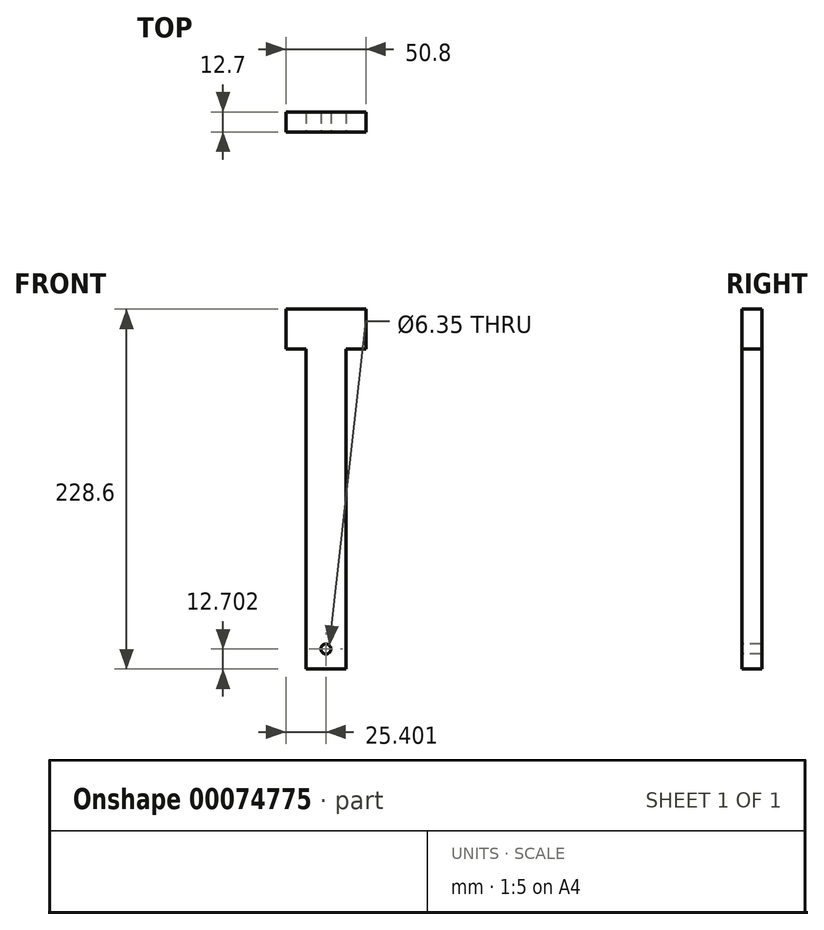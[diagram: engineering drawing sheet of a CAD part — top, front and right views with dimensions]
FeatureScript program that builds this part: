
annotation { "Feature Type Name" : "Feature", "Feature Type Description" : "" }
export const myFeature = defineFeature(function(context is Context, id is Id, definition is map)
    precondition{}
    {
        {
            var Q0;
            Q0=qCreatedBy(makeId("Front.planeOp"),FACE);
            var sketch = newSketch(context, id + "F0", { "sketchPlane" : qUnion([Q0])});
            skLineSegment(sketch, "E0", {"start": v(-30.38, -174.97) * mm, "end": v(-4.98, -174.97) * mm});
            skLineSegment(sketch, "E1", {"start": v(-4.98, -174.97) * mm, "end": v(-4.98, 28.23) * mm});
            skLineSegment(sketch, "E2", {"start": v(-4.98, 28.23) * mm, "end": v(7.72, 28.23) * mm});
            skLineSegment(sketch, "E3", {"start": v(7.72, 28.23) * mm, "end": v(7.72, 53.63) * mm});
            skLineSegment(sketch, "E4", {"start": v(7.72, 53.63) * mm, "end": v(-43.08, 53.63) * mm});
            skLineSegment(sketch, "E5", {"start": v(-43.08, 53.63) * mm, "end": v(-43.08, 28.23) * mm});
            skLineSegment(sketch, "E6", {"start": v(-43.08, 28.23) * mm, "end": v(-30.38, 28.23) * mm});
            skLineSegment(sketch, "E7", {"start": v(-30.38, 28.23) * mm, "end": v(-30.38, -174.97) * mm});
            skSolve(sketch);
        }
        {
            var Q0;
            Q0=makeQuery(id+"F0.imprint","IMPRINT",FACE,{"disambiguationData":[TD([[makeQuery(id+"F0.imprint","IMPRINT",EDGE,{"derivedFrom":sQuery(id+"F0.wireOp",EDGE,"E0")}),1.0]])]});
            extrude(context, id + "F1", {"entities" : qUnion([Q0]), "oppositeDirection" : true, "depth" : 12.7 * mm});
        }
        {
            var Q0;
            Q0=makeQuery(id+"F1.opExtrude","CAP_FACE",FACE,{"disambiguationData":[OSD([sQuery(id+"F0.wireOp",EDGE,"E0"),sQuery(id+"F0.wireOp",EDGE,"E1"),sQuery(id+"F0.wireOp",EDGE,"E2"),sQuery(id+"F0.wireOp",EDGE,"E3"),sQuery(id+"F0.wireOp",EDGE,"E4"),sQuery(id+"F0.wireOp",EDGE,"E5"),sQuery(id+"F0.wireOp",EDGE,"E6"),sQuery(id+"F0.wireOp",EDGE,"E7")])],"isStart":true});
            var sketch = newSketch(context, id + "F2", { "sketchPlane" : qUnion([Q0])});
            skPoint(sketch, "E8", {"position": v(-17.68, -162.27) * mm});
            skPoint(sketch, "E8.positionSnap0", {"position": v(-17.68, -174.97) * mm});
            skSolve(sketch);
        }
        {
            var Q0;
            Q0=sQuery(id+"F2.wireOp",VERTEX,"E8");
            var Q1;
            Q1=makeQuery(id+"F1.opExtrude","SWEPT_BODY",BODY,{"disambiguationData":[OSD([sQuery(id+"F0.wireOp",EDGE,"E0"),sQuery(id+"F0.wireOp",EDGE,"E1"),sQuery(id+"F0.wireOp",EDGE,"E2"),sQuery(id+"F0.wireOp",EDGE,"E3"),sQuery(id+"F0.wireOp",EDGE,"E4"),sQuery(id+"F0.wireOp",EDGE,"E5"),sQuery(id+"F0.wireOp",EDGE,"E6"),sQuery(id+"F0.wireOp",EDGE,"E7")])]});
            hole(context, id + "F3", {"style" : HoleStyle.SIMPLE, "holeDiameter" : 6.35 * mm, "endStyle" : HoleEndStyle.THROUGH, "locations" : qUnion([Q0]), "scope" : qUnion([Q1])});
        }
    });
